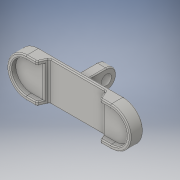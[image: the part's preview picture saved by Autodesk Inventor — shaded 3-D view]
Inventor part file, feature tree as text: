
AUTODESK INVENTOR PART (.ipt)
format: ipt  version: 2016 (Build 200138000, 138)  size: 445,440 bytes
history: native  units: in
note: dims shown in document units (in); Inventor stores cm internally (conversion verified against a paired STEP export)
features: fillet x8, extrude x6, sketch x6, chamfer x1
ambient origin geometry x8: Origin, YZ Plane, XZ Plane, XY Plane, X Axis, Y Axis, Z Axis, Center Point
bodies: Solid1 (feature_tree)
feature tree (21):
  extrude  "Extrusion1"  Depth=0.75in
  fillet  "Fillet1"  Radius=0.25in
  extrude  "Extrusion2"  Depth=2.9in
  extrude  "Extrusion3"  Depth=1.325in
  extrude  "Extrusion4"  Depth=0.39in
  fillet  "Fillet2"  Radius=0.2in
  fillet  "Fillet3"  [1 undecoded]
  extrude  "Extrusion5"  Depth=0.1in
  fillet  "Fillet5"  Radius=0.1in
  fillet  "Fillet6"  Radius=0.325in
  extrude  "Extrusion6"  Depth=0.05in
  fillet  "Fillet7"  Radius=0.7in
  chamfer  "Chamfer1"  Distance=0.225in
  fillet  "Fillet8"  [1 undecoded]
  fillet  "Fillet9"  Radius=0.1in
  sketch  "Sketch1"  dims[d0=0.5in d1=0.75in d2=0.25in d3=0.0in]
  sketch  "Sketch2"  dims[d4=0.25in d5=2.9in]
  sketch  "Sketch3"  dims[d6=0.78in d7=1.325in]
  sketch  "Sketch4"  dims[d8=0.0in d9=0.39in d10=0.2in d11=0.0in d12=0.0in]
  sketch  "Sketch5"  dims[d13=0.0in d14=0.39in d15=0.1in d16=0.325in d17=0.0in]
  sketch  "Sketch6"  dims[d19=0.125in d20=1.4in d21=0.7in d22=0.225in d23=0.0in d24=0.1in d25=1.0in d26=0.0in d27=0.05in d28=0.025in d30=0.25in d31=1.0in d32=0.0in d33=0.025in d34=0.025in d36=0.415in d37=0.15in d38=0.75in d39=1.0in d40=0.0in d41=0.0in d42=0.05in d43=0.2in d44=0.1in d45=0.125in d46=45.0deg d47=0.05in d48=0.05in]
note: 2 required parameter values undecoded (feature->parameter linkage not recoverable at this tier; creation-order binding heuristic only, values carry confidence <= 0.55)
